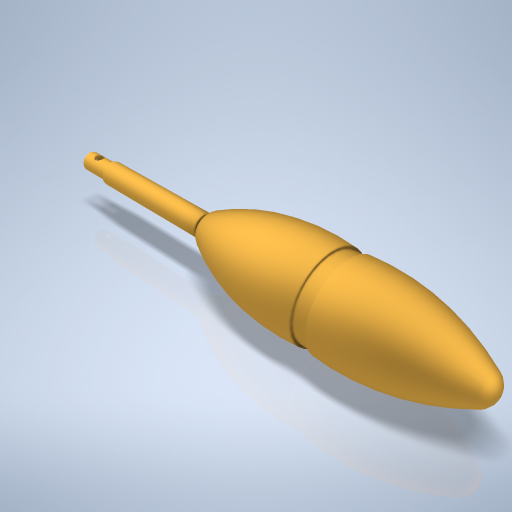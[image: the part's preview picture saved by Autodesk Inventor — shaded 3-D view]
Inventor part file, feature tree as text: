
AUTODESK INVENTOR PART (.ipt)
format: ipt  version: 2024.2 (Build 282272000, 272)  size: 397,824 bytes
history: native  units: mm
features: sketch x7, revolve x5, plane x2, projected_geometry x2, hole x1, extrude x1
ambient origin geometry x8: Origin, YZ Plane, XZ Plane, XY Plane, X Axis, Y Axis, Z Axis, Center Point
bodies: Volumenkörper1 (feature_tree)
feature tree (18):
  revolve  "Umdrehung1"
  plane  "Arbeitsebene1"
  revolve  "Umdrehung7"
  revolve  "Umdrehung8"
  hole  "Bohrung1"  [1 undecoded]
  revolve  "Umdrehung10"
  revolve  "Umdrehung11"
  plane  "Arbeitsebene2"
  extrude  "Extrusion1"  Depth=4.0mm
  sketch  "Skizze1"  dims[d0=29.0mm d1=1.21mm]
  sketch  "Skizze8"  dims[d2=7.0mm d3=4.0mm]
  projected_geometry  "Projizierte Kontur4"
  sketch  "Skizze9"  dims[d4=45.0mm]
  sketch  "Skizze10"  dims[d5=18.0mm]
  sketch  "Skizze13"  dims[d6=0.686853mm]
  sketch  "Skizze15"  dims[d7=90.0deg]
  projected_geometry  "Projizierte Kontur6"
  sketch  "Skizze18"  dims[d8=0.0mm d56=5.99mm d57=4.0mm d60=17.0mm d61=11.0mm d62=90.0deg d63=6.0mm d64=40.0mm d65=5.0mm d66=7.0mm d67=90.0deg d68=2.5mm d69=6.0mm d70=4.0mm d71=2.0mm d72=90.0deg d73=50.0mm d74=0.0mm d92=3.5mm d93=18.0mm d94=17.0mm d95=30.5mm d96=45.0mm d97=3.0mm d98=90.0deg d99=16.0mm d100=90.0deg d101=0.0mm d102=2.0mm d103=3.0mm d104=3.0mm d105=0.0mm d43=0.872665mm d44=0.872665mm d55=0.872665mm]
note: 1 required parameter value undecoded (feature->parameter linkage not recoverable at this tier; creation-order binding heuristic only, values carry confidence <= 0.55)
